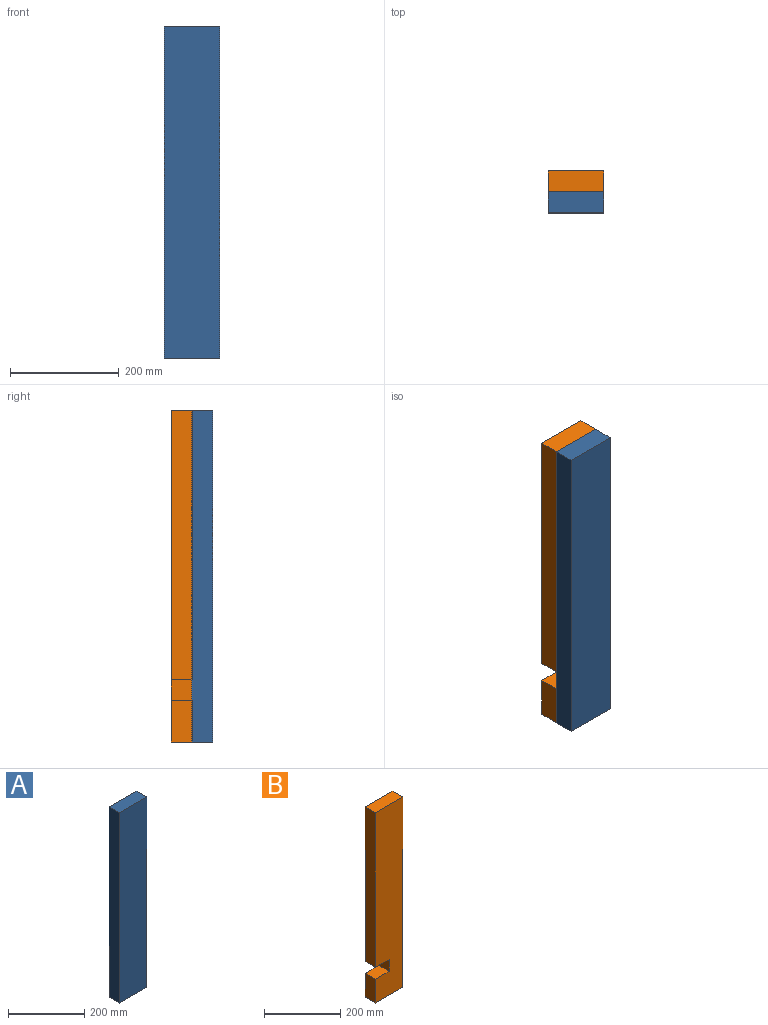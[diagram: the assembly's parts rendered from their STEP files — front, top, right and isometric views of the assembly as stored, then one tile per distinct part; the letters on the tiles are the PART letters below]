
ASSEMBLY  parts=2 mates=1
PART A: 6 faces, bbox 101.6x38.1x609.6 mm
  f0: plane 609.6x38.1mm, normal (-1,0,0), area 23225.8mm2, adj f1,f3,f4,f5
  f1: plane 609.6x101.6mm, normal (0,-1,0), area 61935.4mm2, adj f0,f2,f4,f5
  f2: plane 609.6x38.1mm, normal (1,0,0), area 23225.8mm2, adj f1,f3,f4,f5
  f3: plane 609.6x101.6mm, normal (0,1,0), area 61935.4mm2, adj f0,f2,f4,f5
  f4: plane 101.6x38.1mm, normal (0,0,1), area 3871mm2, adj f0,f1,f2,f3
  f5: plane 101.6x38.1mm, normal (0,0,-1), area 3871mm2, adj f0,f1,f2,f3
PART B: 10 faces, bbox 101.6x38.1x609.6 mm
  f0: plane 495.3x38.1mm, normal (-1,0,0), area 18870.9mm2, adj f1,f4,f5,f9
  f1: plane 609.6x101.6mm, normal (0,-1,0), area 59999.9mm2, adj f0,f2,f3,f5,f6,f7,f8,f9
  f2: plane 76.2x38.1mm, normal (-1,0,0), area 2903.2mm2, adj f1,f4,f6,f7
  f3: plane 609.6x38.1mm, normal (1,0,0), area 23225.8mm2, adj f1,f4,f5,f6
  f4: plane 609.6x101.6mm, normal (0,1,0), area 59999.9mm2, adj f0,f2,f3,f5,f6,f7,f8,f9
  f5: plane 101.6x38.1mm, normal (0,0,1), area 3871mm2, adj f0,f1,f3,f4
  f6: plane 101.6x38.1mm, normal (0,0,-1), area 3871mm2, adj f1,f2,f3,f4
  f7: plane 50.8x38.1mm, normal (0,0,1), area 1935.5mm2, adj f1,f2,f4,f8
  f8: plane 38.1x38.1mm, normal (-1,0,0), area 1451.6mm2, adj f1,f4,f7,f9
  f9: plane 50.8x38.1mm, normal (0,0,-1), area 1935.5mm2, adj f0,f1,f4,f8
PLACE A t=(-50.8,-19.05,0)mm
PLACE B t=(-50.8,19.05,0)mm
MATE fastened A.f3 <-> B.f1  axis (0,1,0) through (0,19.05,609.6)mm
